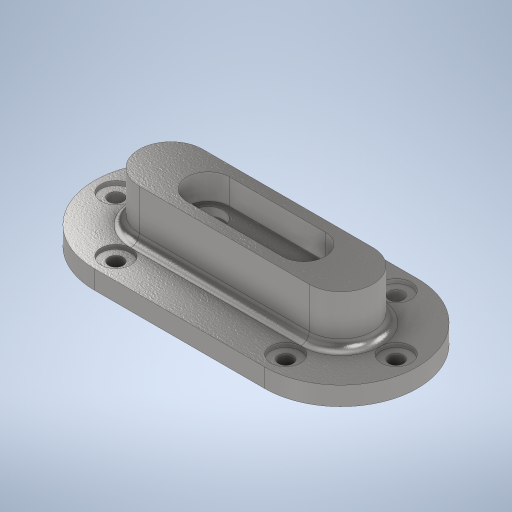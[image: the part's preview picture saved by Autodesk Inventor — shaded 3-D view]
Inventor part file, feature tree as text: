
AUTODESK INVENTOR PART (.ipt)
format: ipt  version: 2024 (Build 280153000, 153)  size: 396,288 bytes
history: native  units: mm
features: sketch x5, extrude x3, hole x3, fillet x1, projected_geometry x1
ambient origin geometry x8: Origin, YZ Plane, XZ Plane, XY Plane, X Axis, Y Axis, Z Axis, Center Point
bodies: Volumenkörper1 (feature_tree)
feature tree (13):
  extrude  "Extrusion1"  Depth=18.0mm
  sketch  "Skizze2"  dims[d2=40.0mm d3=4.4mm d4=0.0mm]
  extrude  "Extrusion3"  Depth=4.4mm TaperAngle=0.0deg
  extrude  "Extrusion4"  Depth=5.0mm
  fillet  "Rundung1"  Radius=7.5mm
  hole  "Bohrung1"  [1 undecoded]
  hole  "Bohrung2"  [1 undecoded]
  hole  "Bohrung3"  [1 undecoded]
  sketch  "Skizze1"  dims[d0=36.0mm d1=18.0mm]
  sketch  "Skizze3"  dims[d5=22.5mm d6=5.0mm d7=7.5mm]
  sketch  "Skizze4"  dims[d10=5.6mm d11=0.0mm d12=11.6mm d13=0.0mm]
  sketch  "Skizze5"  dims[d14=2.0mm d15=5.0mm d16=6.0mm d17=7.0mm d18=2.0mm d19=90.0deg d20=8.0mm d21=0.0mm d22=5.0mm d23=6.0mm d24=7.0mm d25=2.0mm d26=90.0deg d27=8.0mm d28=0.0mm d30=13.0mm d32=3.4mm d33=6.0mm d34=7.0mm d35=1.0mm d36=90.0deg d37=8.0mm d38=0.0mm d29=1.0mm d31=1.0mm d39=0.75mm d40=0.375mm d41=1.0mm d42=0.15mm d43=0.25mm d44=0.375mm d45=14.3117mm d46=0.75mm d47=20.594885mm d48=0.0625mm d49=0.75mm d50=0.375mm]
  projected_geometry  "Projizierte Kontur1"
note: 3 required parameter values undecoded (feature->parameter linkage not recoverable at this tier; creation-order binding heuristic only, values carry confidence <= 0.55)
